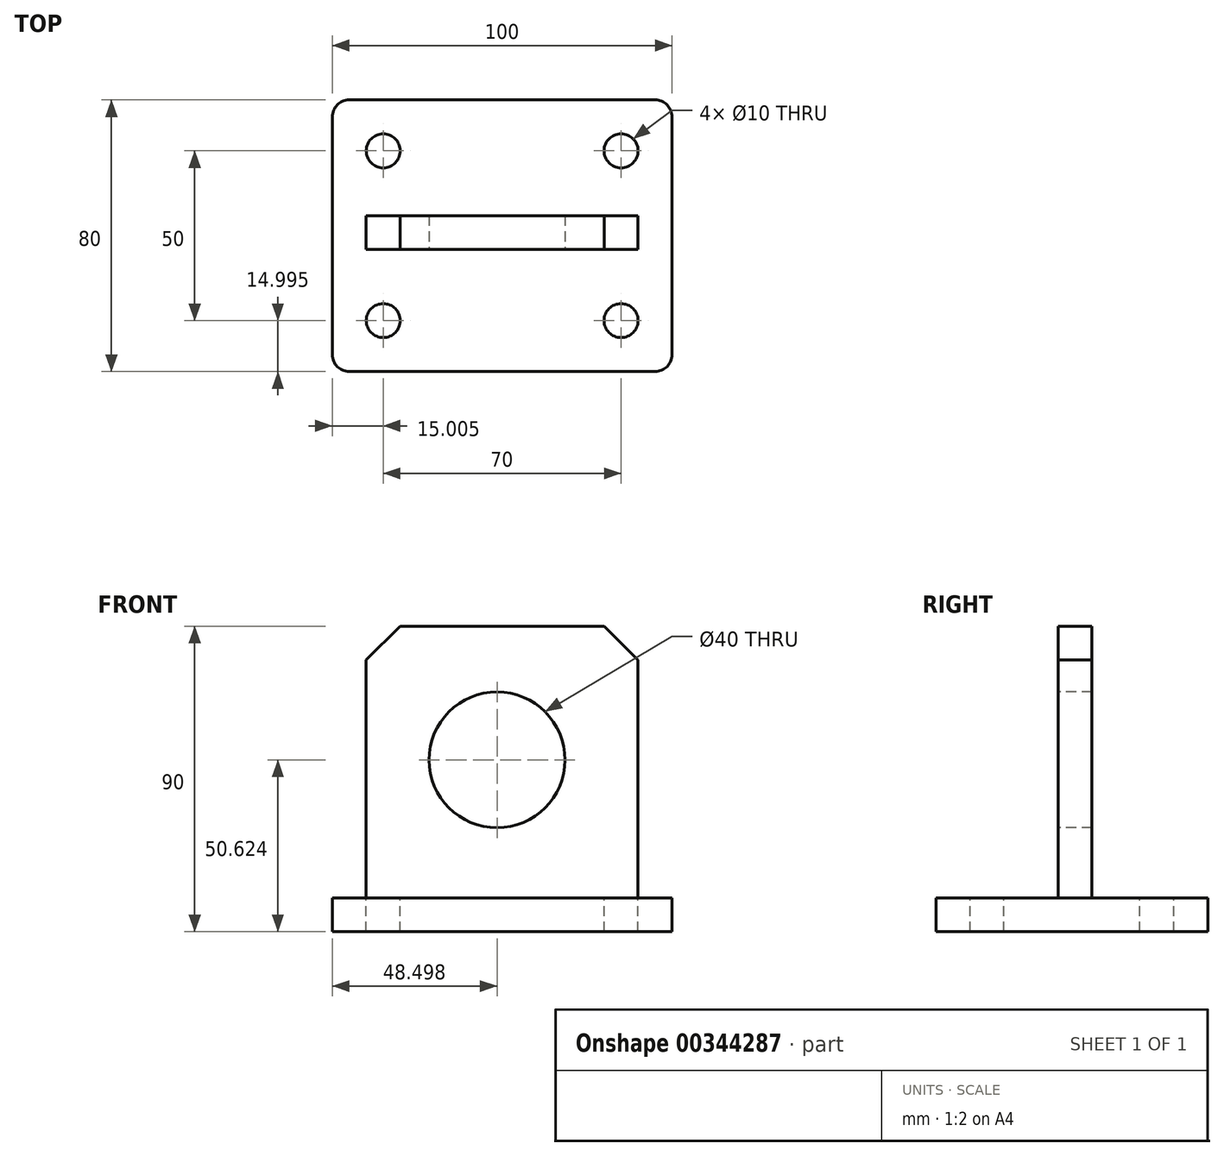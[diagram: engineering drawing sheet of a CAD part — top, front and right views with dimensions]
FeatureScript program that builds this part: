
annotation { "Feature Type Name" : "Feature", "Feature Type Description" : "" }
export const myFeature = defineFeature(function(context is Context, id is Id, definition is map)
    precondition{}
    {
        {
            var Q0;
            Q0=qCreatedBy(makeId("Top.planeOp"),FACE);
            var sketch = newSketch(context, id + "F0", { "sketchPlane" : qUnion([Q0])});
            skLineSegment(sketch, "E0.bottom", {"start": v(-36.45, 34.09) * mm, "end": v(63.55, 34.09) * mm});
            skLineSegment(sketch, "E0.top", {"start": v(-36.45, -45.91) * mm, "end": v(63.55, -45.91) * mm});
            skLineSegment(sketch, "E0.left", {"start": v(-36.45, 34.09) * mm, "end": v(-36.45, -45.91) * mm});
            skLineSegment(sketch, "E0.right", {"start": v(63.55, 34.09) * mm, "end": v(63.55, -45.91) * mm});
            skSolve(sketch);
        }
        {
            var Q0;
            Q0=makeQuery(id+"F0.imprint","IMPRINT",FACE,{"disambiguationData":[TD([[makeQuery(id+"F0.imprint","IMPRINT",EDGE,{"derivedFrom":sQuery(id+"F0.wireOp",EDGE,"E0.bottom")}),-1.0]])]});
            extrude(context, id + "F1", {"entities" : qUnion([Q0]), "depth" : 10 * mm});
        }
        {
            var Q0;
            Q0=makeQuery(id+"F1.opExtrude","CAP_FACE",FACE,{"disambiguationData":[OSD([sQuery(id+"F0.wireOp",EDGE,"E0.bottom"),sQuery(id+"F0.wireOp",EDGE,"E0.top"),sQuery(id+"F0.wireOp",EDGE,"E0.left"),sQuery(id+"F0.wireOp",EDGE,"E0.right")])],"isStart":false});
            var sketch = newSketch(context, id + "F2", { "sketchPlane" : qUnion([Q0])});
            skCircle(sketch, "E1", {"center": v(-21.45, 19.09) * mm, "radius": 5 * mm});
            skCircle(sketch, "E2", {"center": v(-21.45, -30.91) * mm, "radius": 5 * mm});
            skCircle(sketch, "E3", {"center": v(48.55, 19.09) * mm, "radius": 5 * mm});
            skCircle(sketch, "E4", {"center": v(48.55, -30.91) * mm, "radius": 5 * mm});
            skSolve(sketch);
        }
        {
            var Q0;
            Q0=sQuery(id+"F2.wireOp",VERTEX,"E2.center");
            var Q1;
            Q1=sQuery(id+"F2.wireOp",VERTEX,"E1.center");
            var Q2;
            Q2=sQuery(id+"F2.wireOp",VERTEX,"E3.center");
            var Q3;
            Q3=sQuery(id+"F2.wireOp",VERTEX,"E4.center");
            var Q4;
            Q4=makeQuery(id+"F1.opExtrude","SWEPT_BODY",BODY,{"disambiguationData":[OSD([sQuery(id+"F0.wireOp",EDGE,"E0.bottom"),sQuery(id+"F0.wireOp",EDGE,"E0.top"),sQuery(id+"F0.wireOp",EDGE,"E0.left"),sQuery(id+"F0.wireOp",EDGE,"E0.right")])]});
            hole(context, id + "F3", {"style" : HoleStyle.SIMPLE, "endStyle" : HoleEndStyle.THROUGH, "holeDiameter" : 10 * mm, "isTappedThrough" : true, "tappedDepth" : 12 * mm, "tapClearance" : 3, "locations" : qUnion([Q0, Q1, Q2, Q3]), "scope" : qUnion([Q4])});
        }
        {
            var Q0;
            Q0=makeQuery(id+"F1.opExtrude","SWEPT_EDGE",EDGE,{"disambiguationData":[OSD([sQuery(id+"F0.wireOp",EDGE,"E0.bottom"),sQuery(id+"F0.wireOp",EDGE,"E0.right")])]});
            fillet(context, id + "F4", {"entities" : qUnion([Q0]), "radius" : 5 * mm, "tangentPropagation" : true, "allowEdgeOverflow" : false});
        }
        {
            var Q0;
            Q0=makeQuery(id+"F1.opExtrude","SWEPT_EDGE",EDGE,{"disambiguationData":[OSD([sQuery(id+"F0.wireOp",EDGE,"E0.top"),sQuery(id+"F0.wireOp",EDGE,"E0.right")])]});
            var Q1;
            Q1=makeQuery(id+"F1.opExtrude","SWEPT_EDGE",EDGE,{"disambiguationData":[OSD([sQuery(id+"F0.wireOp",EDGE,"E0.top"),sQuery(id+"F0.wireOp",EDGE,"E0.left")])]});
            var Q2;
            Q2=makeQuery(id+"F1.opExtrude","SWEPT_EDGE",EDGE,{"disambiguationData":[OSD([sQuery(id+"F0.wireOp",EDGE,"E0.bottom"),sQuery(id+"F0.wireOp",EDGE,"E0.left")])]});
            fillet(context, id + "F5", {"entities" : qUnion([Q0, Q1, Q2]), "radius" : 5 * mm, "tangentPropagation" : true, "allowEdgeOverflow" : false});
        }
        {
            var Q0;
            Q0=makeQuery(id+"F1.opExtrude","CAP_FACE",FACE,{"disambiguationData":[OSD([sQuery(id+"F0.wireOp",EDGE,"E0.bottom"),sQuery(id+"F0.wireOp",EDGE,"E0.top"),sQuery(id+"F0.wireOp",EDGE,"E0.left"),sQuery(id+"F0.wireOp",EDGE,"E0.right")])],"isStart":false});
            var sketch = newSketch(context, id + "F6", { "sketchPlane" : qUnion([Q0])});
            skLineSegment(sketch, "E5.bottom", {"start": v(-26.45, -10) * mm, "end": v(53.55, -10) * mm});
            skLineSegment(sketch, "E5.top", {"start": v(-26.45, 0) * mm, "end": v(53.55, 0) * mm});
            skLineSegment(sketch, "E5.left", {"start": v(-26.45, -10) * mm, "end": v(-26.45, 0) * mm});
            skLineSegment(sketch, "E5.right", {"start": v(53.55, -10) * mm, "end": v(53.55, 0) * mm});
            skSolve(sketch);
        }
        {
            var Q0;
            Q0 = qSketchRegion(id + "F6", true);
            var Q1;
            Q1=makeQuery(id+"F6.imprint","IMPRINT",FACE,{"disambiguationData":[TD([[makeQuery(id+"F6.imprint","IMPRINT",EDGE,{"derivedFrom":sQuery(id+"F6.wireOp",EDGE,"E5.bottom")}),1.0]])]});
            extrude(context, id + "F7", {"entities" : qUnion([Q0, Q1]), "operationType" : NewBodyOperationType.ADD, "depth" : 80 * mm});
        }
        {
            var Q0;
            Q0=makeQuery(id+"F7.opExtrude","CAP_EDGE",EDGE,{"disambiguationData":[OSD([sQuery(id+"F6.wireOp",EDGE,"E5.right")])],"isStart":false});
            var Q1;
            Q1=makeQuery(id+"F7.opExtrude","CAP_EDGE",EDGE,{"disambiguationData":[OSD([sQuery(id+"F6.wireOp",EDGE,"E5.left")])],"isStart":false});
            chamfer(context, id + "F8", {"entities" : qUnion([Q0, Q1]), "width" : 10 * mm, "tangentPropagation" : true});
        }
        {
            var Q0;
            Q0=makeQuery(id+"F7.opExtrude","SWEPT_FACE",FACE,{"disambiguationData":[OSD([sQuery(id+"F6.wireOp",EDGE,"E5.bottom")])]});
            var sketch = newSketch(context, id + "F9", { "sketchPlane" : qUnion([Q0])});
            skCircle(sketch, "E6", {"center": v(12.05, 50.62) * mm, "radius": 12.71 * mm});
            skSolve(sketch);
        }
        {
            var Q0;
            Q0=sQuery(id+"F9.wireOp",VERTEX,"E6.center");
            var Q1;
            Q1=makeQuery(id+"F1.opExtrude","SWEPT_BODY",BODY,{"disambiguationData":[OSD([sQuery(id+"F0.wireOp",EDGE,"E0.bottom"),sQuery(id+"F0.wireOp",EDGE,"E0.top"),sQuery(id+"F0.wireOp",EDGE,"E0.left"),sQuery(id+"F0.wireOp",EDGE,"E0.right")])]});
            hole(context, id + "F10", {"style" : HoleStyle.SIMPLE, "endStyle" : HoleEndStyle.THROUGH, "holeDiameter" : 40 * mm, "isTappedThrough" : true, "tappedDepth" : 12 * mm, "tapClearance" : 3, "locations" : qUnion([Q0]), "scope" : qUnion([Q1])});
        }
    });
